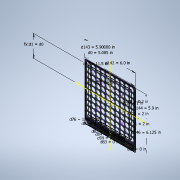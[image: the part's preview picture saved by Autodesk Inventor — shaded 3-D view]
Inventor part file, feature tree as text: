
AUTODESK INVENTOR PART (.ipt)
format: ipt  version: 2020.3 (Build 243373000, 373)  size: 490,496 bytes
history: native  units: in
note: dims shown in document units (in); Inventor stores cm internally (conversion verified against a paired STEP export)
features: hole x4, chamfer x4, sketch x4, fillet x3, extrude x2, pattern_linear x2
ambient origin geometry x8: Origin, YZ Plane, XZ Plane, XY Plane, X Axis, Y Axis, Z Axis, Center Point
bodies: Solid1 (feature_tree)
feature tree (19):
  extrude  "Extrusion1"  Depth=5.085in
  hole  "Hole1"  [1 undecoded]
  chamfer  "Chamfer5"  Distance=4.52in
  pattern_linear  "Rectangular Pattern1"  Spacing1=0.05in  [1 undecoded]
  hole  "Hole8-M4 CSINK"  [1 undecoded]
  pattern_linear  "Rectangular Pattern3"  Spacing1=1.125in  [1 undecoded]
  sketch  "Sketch4"  dims[d0=5.085in d1=5.085in]
  extrude  "Extrusion4"  Depth=0.25in TaperAngle=0.0deg
  hole  "Hole6"  [1 undecoded]
  chamfer  "Chamfer9"  [1 undecoded]
  chamfer  "Chamfer8"  Distance=0.75in
  fillet  "Fillet7"  Radius=0.75in
  hole  "Hole7"  [1 undecoded]
  fillet  "Fillet8"  Radius=0.219in
  chamfer  "Chamfer10"  Distance=0.75in Angle=15.0deg
  fillet  "Fillet9"  Radius=0.25in
  sketch  "Sketch5"  dims[d4=0.2in d5=0.0in]
  sketch  "Sketch6"  dims[d6=1.037in d7=0.3389in d8=1.125in d9=0.1in d10=60.0deg d11=1.0in d12=0.8108in d13=3.937in d15=1.13in d16=3.937in d18=1.13in]
  sketch  "Sketch7"  dims[d23=6.0in d36=4.52in d60=0.05in d61=0.125in d62=60.0deg d63=11.5in d76=1.125in d77=1.0in d78=0.0in d82=7.0in d83=0.0in d84=0.75in d85=0.75in d98=0.0in d99=0.219in d107=0.15in d108=0.75in d109=0.279in d110=0.25in d111=0.5635in d112=1.0in d113=0.8108in d114=0.75in d115=0.125in d116=15.0deg d117=0.25in d118=0.2in d119=1.0in d120=2.0in d121=2.0in d122=0.75in d123=0.125in d124=15.0deg d126=0.7in d127=6.85in d129=0.0968in d130=0.236in d131=0.375in d132=0.25in d133=0.5635in d134=0.346in d135=0.8108in d136=4.0in d137=0.5in d138=1.0in d139=0.125in d140=45.0deg d141=0.25in d142=6.0in d143=5.9in d144=5.9in d146=6.125in d147=3.625in d148=0.177in d149=0.75in d150=0.375in d151=0.25in d152=90.0deg d153=1.0in d154=0.8108in d155=1.9685in d157=2.26in d158=1.9685in d160=2.26in d161=1.0in d162=1.0in]
note: 7 required parameter values undecoded (feature->parameter linkage not recoverable at this tier; creation-order binding heuristic only, values carry confidence <= 0.55)
